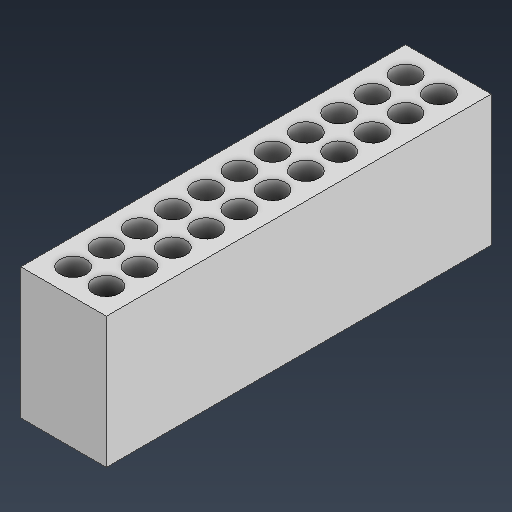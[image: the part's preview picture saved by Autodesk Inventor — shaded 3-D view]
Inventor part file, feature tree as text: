
AUTODESK INVENTOR PART (.ipt)
format: ipt  version: 2025.3 (Build 293356000, 356)  size: 162,304 bytes
history: native  units: mm
features: sketch x2, extrude x1
ambient origin geometry x8: Origin, YZ Plane, XZ Plane, XY Plane, X Axis, Y Axis, Z Axis, Center Point
bodies: Solid1 (feature_tree)
feature tree (3):
  extrude  "Extrusion1"  Depth=2.54mm
  sketch  "Sketch1"  dims[d0=2.0mm d1=20.0mm d3=2.54mm d4=110.0mm d6=2.54mm]
  sketch  "Sketch Rectangular Pattern1"  dims[d9=1.0mm d10=1.0mm d11=1.0mm d12=1.0mm d13=10.0mm d14=0.0mm]
